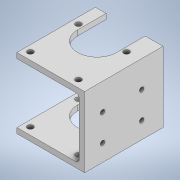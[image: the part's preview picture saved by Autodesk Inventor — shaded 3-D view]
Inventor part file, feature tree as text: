
AUTODESK INVENTOR PART (.ipt)
format: ipt  version: 2022 (Build 260153000, 153)  size: 186,880 bytes
history: native  units: mm
features: sketch x6, extrude x3, hole x3, other x1, fillet x1
ambient origin geometry x8: Origin, YZ Plane, XZ Plane, XY Plane, X Axis, Y Axis, Z Axis, Center Point
bodies: Body1 (feature_tree)
feature tree (14):
  other  "ソリッド1"
  extrude  "押し出し1"  Depth=44.0mm
  extrude  "押し出し2"  Depth=38.0mm
  hole  "穴1"  [1 undecoded]
  hole  "穴2"  [1 undecoded]
  fillet  "フィレット1"  Radius=3.0mm
  extrude  "押し出し3"  Depth=3.0mm
  hole  "穴5"  [1 undecoded]
  sketch  "スケッチ1"
  sketch  "スケッチ2"
  sketch  "スケッチ3"
  sketch  "スケッチ4"
  sketch  "スケッチ7"
  sketch  "スケッチ8"
note: 3 required parameter values undecoded (feature->parameter linkage not recoverable at this tier; creation-order binding heuristic only, values carry confidence <= 0.55)
